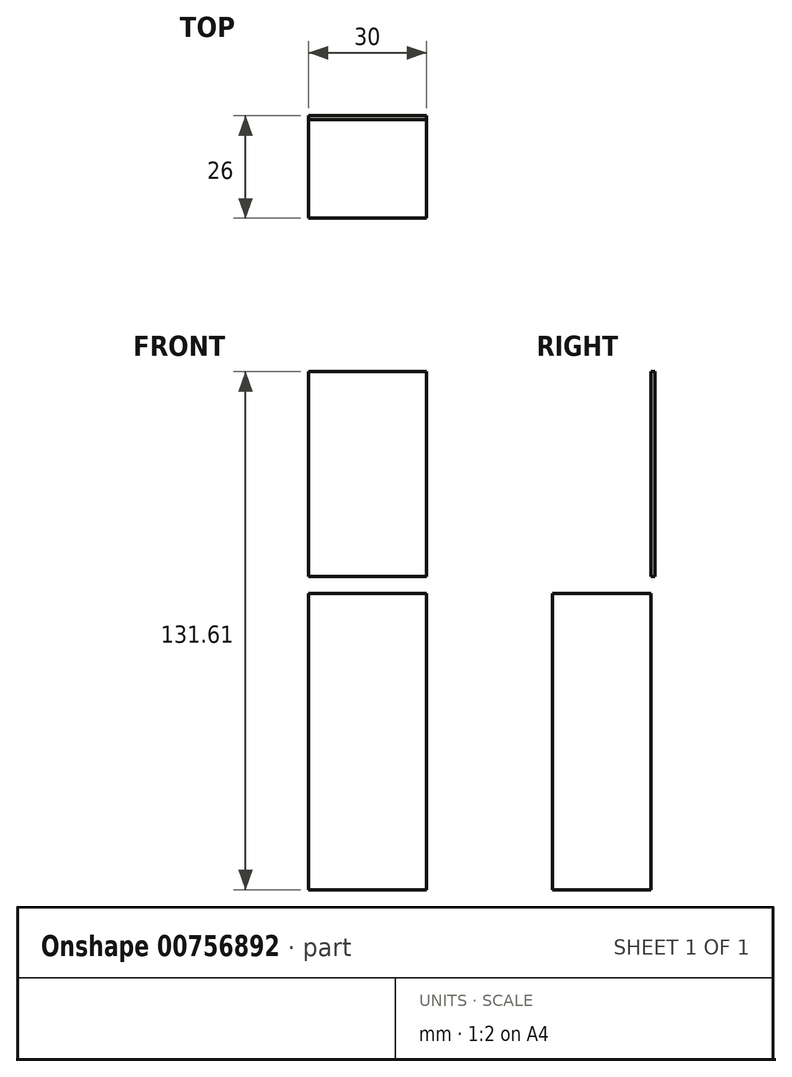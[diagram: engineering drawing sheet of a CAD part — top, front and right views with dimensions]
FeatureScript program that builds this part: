
annotation { "Feature Type Name" : "Feature", "Feature Type Description" : "" }
export const myFeature = defineFeature(function(context is Context, id is Id, definition is map)
    precondition{}
    {
        {
            var Q0;
            Q0=qCreatedBy(makeId("Front.planeOp"),FACE);
            var sketch = newSketch(context, id + "F0", { "sketchPlane" : qUnion([Q0])});
            skLineSegment(sketch, "E0.bottom", {"start": v(0, -46.88) * mm, "end": v(-30, -46.88) * mm});
            skLineSegment(sketch, "E0.top", {"start": v(0, 28.42) * mm, "end": v(-30, 28.42) * mm});
            skLineSegment(sketch, "E0.left", {"start": v(0, -46.88) * mm, "end": v(0, 28.42) * mm});
            skLineSegment(sketch, "E0.right", {"start": v(-30, -46.88) * mm, "end": v(-30, 28.42) * mm});
            skPoint(sketch, "E0.middle", {"position": v(-15, -9.23) * mm});
            skPoint(sketch, "E1", {"position": v(-30, 20.62) * mm});
            skPoint(sketch, "E2", {"position": v(0, 20.62) * mm});
            skSolve(sketch);
        }
        {
            var Q0;
            Q0 = qSketchRegion(id + "F0", true);
            extrude(context, id + "F1", {"entities" : qUnion([Q0]), "depth" : 25 * mm, "offsetDistance" : 25 * mm});
        }
        {
            var Q0;
            Q0=qCreatedBy(makeId("Front.planeOp"),FACE);
            var sketch = newSketch(context, id + "F2", { "sketchPlane" : qUnion([Q0])});
            skLineSegment(sketch, "E3.bottom", {"start": v(-30, 32.73) * mm, "end": v(0, 32.73) * mm});
            skLineSegment(sketch, "E3.top", {"start": v(-30, 84.73) * mm, "end": v(0, 84.73) * mm});
            skLineSegment(sketch, "E3.left", {"start": v(-30, 32.73) * mm, "end": v(-30, 84.73) * mm});
            skLineSegment(sketch, "E3.right", {"start": v(0, 32.73) * mm, "end": v(0, 84.73) * mm});
            skPoint(sketch, "E4", {"position": v(-15, 84.73) * mm});
            skPoint(sketch, "E5", {"position": v(-15, 32.73) * mm});
            skPoint(sketch, "E6", {"position": v(-30, 60.99) * mm});
            skPoint(sketch, "E7", {"position": v(0, 60.99) * mm});
            skSolve(sketch);
        }
        {
            var Q0;
            Q0 = qSketchRegion(id + "F2", true);
            extrude(context, id + "F3", {"entities" : qUnion([Q0]), "oppositeDirection" : true, "depth" : 1 * mm, "offsetDistance" : 25 * mm});
        }
    });
